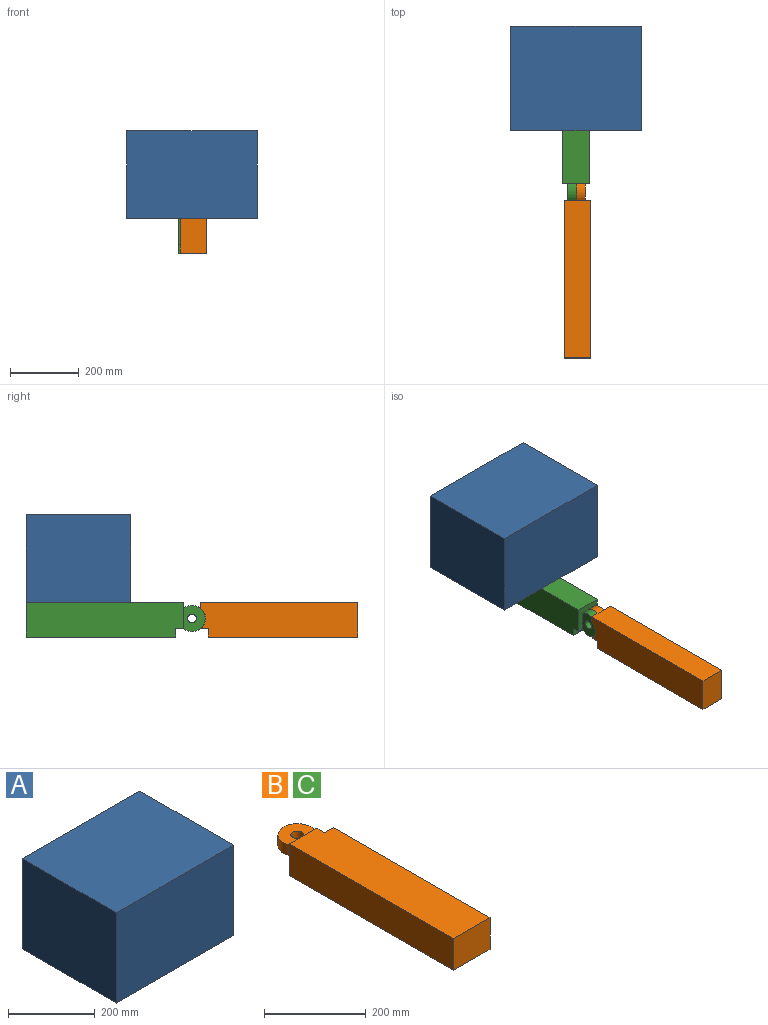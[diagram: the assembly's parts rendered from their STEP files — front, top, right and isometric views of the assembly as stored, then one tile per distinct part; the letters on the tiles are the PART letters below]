
ASSEMBLY  parts=3 mates=2
PART A: 6 faces, bbox 381x304.8x254 mm
  f0: plane 381x254mm, normal (0,1,0), area 96774mm2, adj f1,f3,f4,f5
  f1: plane 304.8x254mm, normal (-1,0,0), area 77419.2mm2, adj f0,f2,f4,f5
  f2: plane 381x254mm, normal (0,-1,0), area 96774mm2, adj f1,f3,f4,f5
  f3: plane 304.8x254mm, normal (1,0,0), area 77419.2mm2, adj f0,f2,f4,f5
  f4: plane 381x304.8mm, normal (0,0,1), area 116128.8mm2, adj f0,f1,f2,f3
  f5: plane 381x304.8mm, normal (0,0,-1), area 116128.8mm2, adj f0,f1,f2,f3
PART B: 13 faces, bbox 101.6x520.7x76.2 mm
  f0: plane 76.27x76.2mm, normal (0,1,0), area 2223.3mm2, adj f1,f2,f3,f5,f8,f9,f10,f11
  f1: plane 76.2x63.5mm, normal (0,0,1), area 3554.1mm2, adj f0,f2,f4
  f2: cylinder r=38.1mm len=76.2mm, axis (0,0,1), area 4452.6mm2, adj f0,f1,f3
  f3: plane 77.47x76.2mm, normal (0,0,-1), area 4137mm2, adj f0,f2,f4,f10,f11
  f4: cylinder r=12.7mm len=25.4mm, axis (0,0,1), area 2026.8mm2, adj f1,f3
  f5: plane 457.2x76.2mm, normal (-1,0,0), area 34838.6mm2, adj f0,f6,f8,f9
  f6: plane 101.6x76.2mm, normal (0,-1,0), area 7741.9mm2, adj f5,f7,f8,f9
  f7: plane 435.22x76.2mm, normal (1,0,0), area 33163.5mm2, adj f6,f8,f9,f12
  f8: plane 457.2x101.6mm, normal (0,0,1), area 45894.6mm2, adj f0,f5,f6,f7,f11,f12
  f9: plane 457.2x101.6mm, normal (0,0,-1), area 45311.7mm2, adj f0,f5,f6,f7,f10,f11,f12
  f10: cylinder r=39.37mm len=58.95mm, axis (0,0,1), area 2425.7mm2, adj f0,f3,f9,f11
  f11: plane 76.2x21.98mm, normal (1,0,0), area 1625.5mm2, adj f0,f3,f8,f9,f10,f12
  f12: plane 76.2x25.33mm, normal (0,1,0), area 1930.2mm2, adj f7,f8,f9,f11
PART C: same geometry as B
PLACE A t=(226.27,50.09,161.46)mm
PLACE B rot(axis=(0,1,0),90deg) t=(78.8,-382.76,87)mm
PLACE C rot(axis=(0.71,0,-0.71),180deg) t=(151.6,110.14,87)mm
MATE pin_slot C.f2 <-> B.f2  axis (1,0,0) through (115.2,-136.31,114.07)mm
MATE fastened A.f5 <-> C.f5  axis (0,0,-1) through (113.5,193.89,161.46)mm
